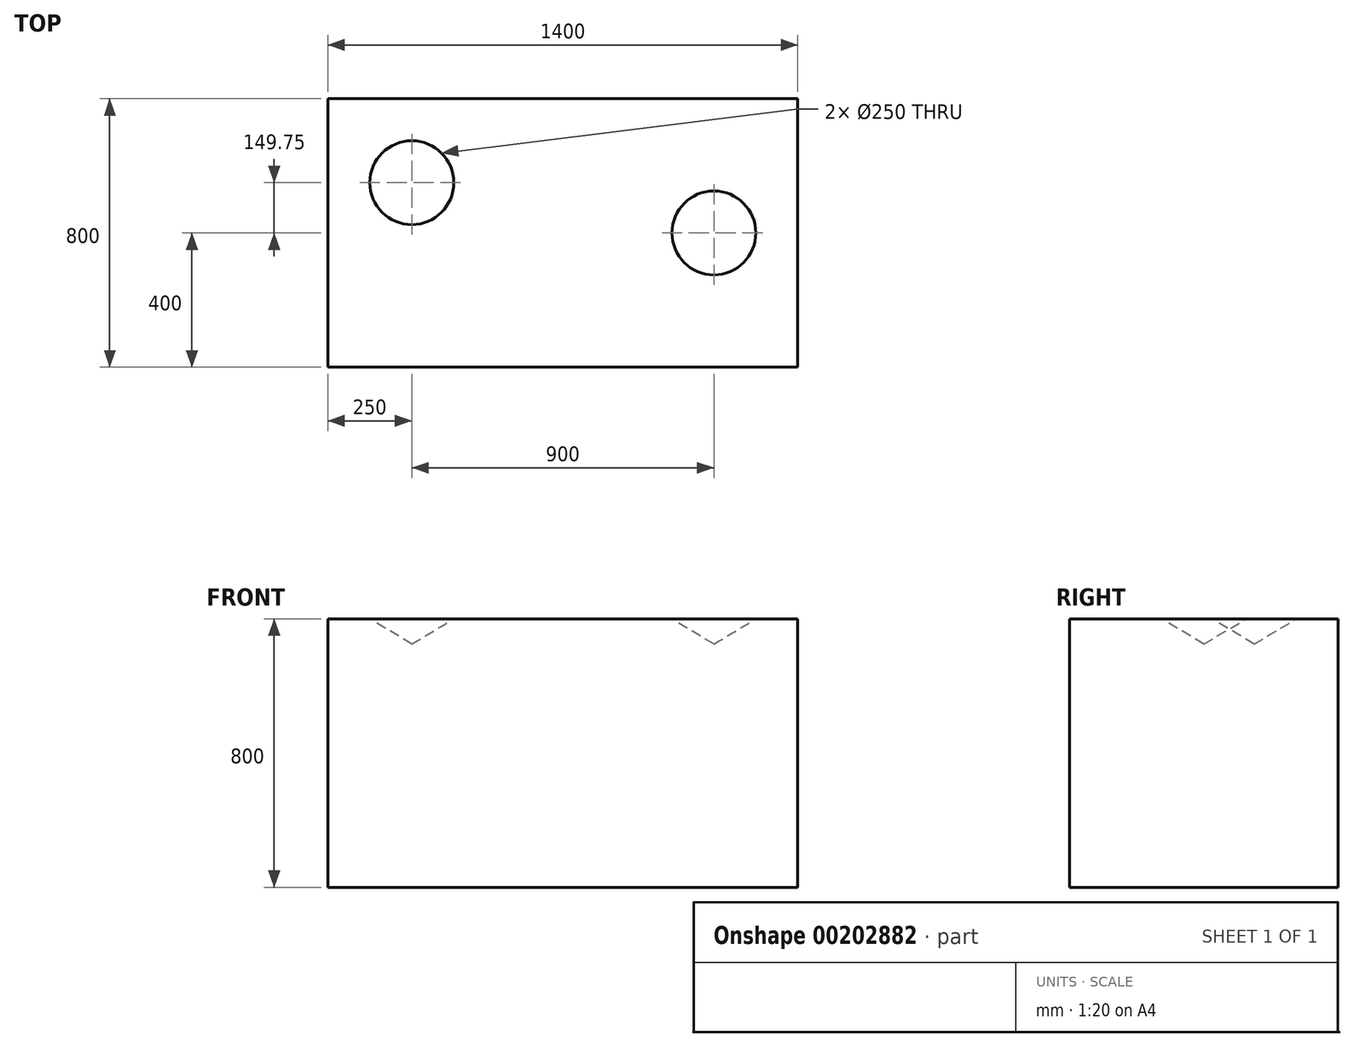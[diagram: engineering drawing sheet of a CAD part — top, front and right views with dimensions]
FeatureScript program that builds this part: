
annotation { "Feature Type Name" : "Feature", "Feature Type Description" : "" }
export const myFeature = defineFeature(function(context is Context, id is Id, definition is map)
    precondition{}
    {
        {
            var Q0;
            Q0=qCreatedBy(makeId("Top.planeOp"),FACE);
            var sketch = newSketch(context, id + "F0", { "sketchPlane" : qUnion([Q0])});
            skLineSegment(sketch, "E0.bottom", {"start": v(700, 400) * mm, "end": v(-700, 400) * mm});
            skLineSegment(sketch, "E0.top", {"start": v(700, -400) * mm, "end": v(-700, -400) * mm});
            skLineSegment(sketch, "E0.left", {"start": v(700, 400) * mm, "end": v(700, -400) * mm});
            skLineSegment(sketch, "E0.right", {"start": v(-700, 400) * mm, "end": v(-700, -400) * mm});
            skPoint(sketch, "E0.middle", {"position": v(0, 0) * mm});
            skSolve(sketch);
        }
        {
            var Q0;
            Q0 = qSketchRegion(id + "F0", true);
            extrude(context, id + "F1", {"entities" : qUnion([Q0]), "depth" : 800 * mm});
        }
        {
            var Q0;
            Q0=makeQuery(id+"F1.opExtrude","CAP_FACE",FACE,{"disambiguationData":[OSD([sQuery(id+"F0.wireOp",EDGE,"E0.bottom"),sQuery(id+"F0.wireOp",EDGE,"E0.top"),sQuery(id+"F0.wireOp",EDGE,"E0.left"),sQuery(id+"F0.wireOp",EDGE,"E0.right")])],"isStart":false});
            var sketch = newSketch(context, id + "F2", { "sketchPlane" : qUnion([Q0])});
            skPoint(sketch, "E1", {"position": v(-450, 149.75) * mm});
            skPoint(sketch, "E2", {"position": v(450, 0) * mm});
            skSolve(sketch);
        }
        {
            var Q0;
            Q0=sQuery(id+"F2.wireOp",VERTEX,"E1");
            var Q1;
            Q1=sQuery(id+"F2.wireOp",VERTEX,"E2");
            var Q2;
            Q2=makeQuery(id+"F1.opExtrude","SWEPT_BODY",BODY,{"disambiguationData":[OSD([sQuery(id+"F0.wireOp",EDGE,"E0.bottom"),sQuery(id+"F0.wireOp",EDGE,"E0.top"),sQuery(id+"F0.wireOp",EDGE,"E0.left"),sQuery(id+"F0.wireOp",EDGE,"E0.right")])]});
            hole(context, id + "F3", {"style" : HoleStyle.SIMPLE, "endStyle" : HoleEndStyle.BLIND, "holeDiameter" : 250 * mm, "holeDepth" : 0.25 * mm, "locations" : qUnion([Q0, Q1]), "scope" : qUnion([Q2])});
        }
    });
